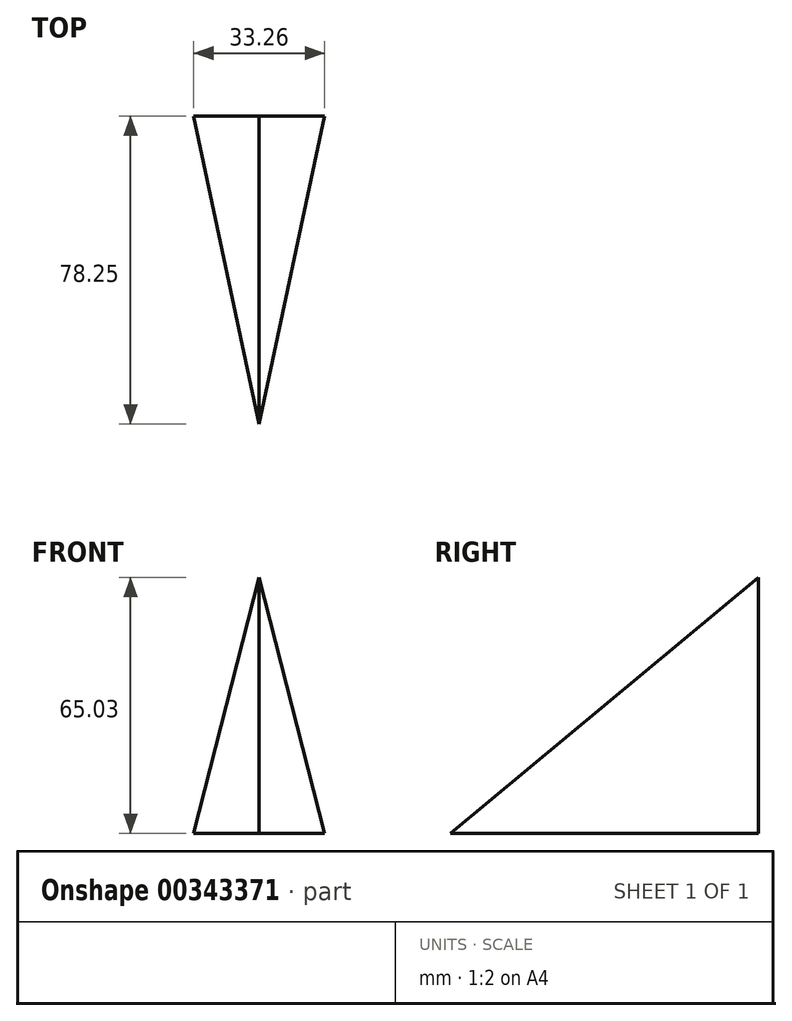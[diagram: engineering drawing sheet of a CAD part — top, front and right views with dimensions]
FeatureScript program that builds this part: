
annotation { "Feature Type Name" : "Feature", "Feature Type Description" : "" }
export const myFeature = defineFeature(function(context is Context, id is Id, definition is map)
    precondition{}
    {
        {
            var Q0;
            Q0=qCreatedBy(makeId("Top.planeOp"),FACE);
            var sketch = newSketch(context, id + "F0", { "sketchPlane" : qUnion([Q0])});
            skLineSegment(sketch, "E0", {"start": v(-16.63, 0) * mm, "end": v(0, -78.25) * mm});
            skLineSegment(sketch, "E1", {"start": v(0, -78.25) * mm, "end": v(16.63, 0) * mm});
            skLineSegment(sketch, "E2", {"start": v(16.63, 0) * mm, "end": v(-16.63, 0) * mm});
            skLineSegment(sketch, "E3", {"start": v(0, 0) * mm, "end": v(16.63, 0) * mm, "construction": true});
            skLineSegment(sketch, "E4", {"start": v(0, 0) * mm, "end": v(0, -78.25) * mm, "construction": true});
            skSolve(sketch);
        }
        {
            var Q0;
            Q0=qCreatedBy(makeId("Front.planeOp"),FACE);
            var sketch = newSketch(context, id + "F1", { "sketchPlane" : qUnion([Q0])});
            skLineSegment(sketch, "E5", {"start": v(0, 0) * mm, "end": v(0, 65.03) * mm});
            skSolve(sketch);
        }
        {
            var Q0;
            Q0 = qSketchRegion(id + "F0", true);
            var Q1;
            Q1=sQuery(id+"F1.wireOp",VERTEX,"E5.end");
            loft(context, id + "F2", {"sheetProfilesArray" : [{ "sheetProfileEntities" : qUnion([Q0]) }, { "sheetProfileEntities" : qUnion([Q1]) }]});
        }
    });
